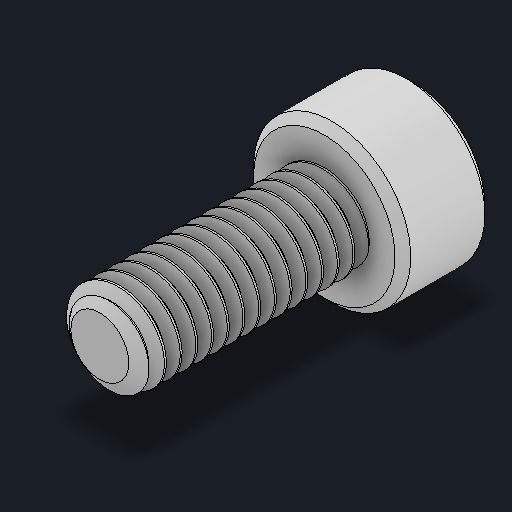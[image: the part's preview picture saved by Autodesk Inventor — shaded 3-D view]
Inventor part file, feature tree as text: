
AUTODESK INVENTOR PART (.ipt)
format: ipt  version: 2024 (Build 280153000, 153)  size: 538,112 bytes
history: native  units: in
note: dims shown in document units (in); Inventor stores cm internally (conversion verified against a paired STEP export)
features: chamfer x1
ambient origin geometry x8: Origin, YZ Plane, XZ Plane, XY Plane, X Axis, Y Axis, Z Axis, Center Point
bodies: Solid1 (feature_tree)
feature tree (1):
  chamfer  "Chamfer1"  [1 undecoded]
note: 1 required parameter value undecoded (feature->parameter linkage not recoverable at this tier; creation-order binding heuristic only, values carry confidence <= 0.55)
